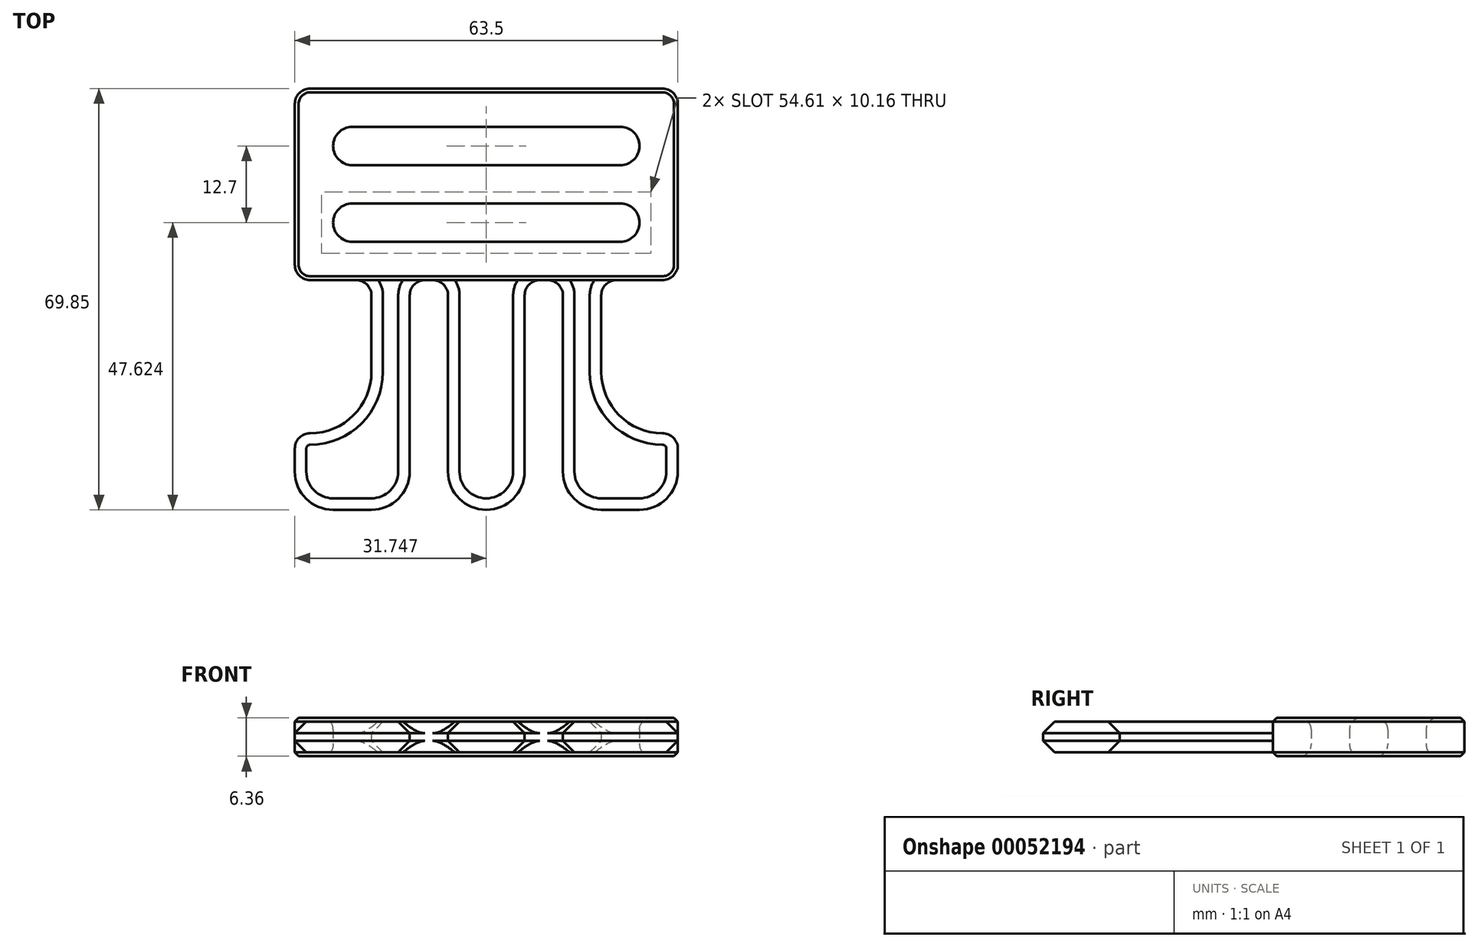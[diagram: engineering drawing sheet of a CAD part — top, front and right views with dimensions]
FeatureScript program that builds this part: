
annotation { "Feature Type Name" : "Feature", "Feature Type Description" : "" }
export const myFeature = defineFeature(function(context is Context, id is Id, definition is map)
    precondition{}
    {
        {
            var Q0;
            Q0=qCreatedBy(makeId("Top.planeOp"),FACE);
            var sketch = newSketch(context, id + "F0", { "sketchPlane" : qUnion([Q0])});
            skLineSegment(sketch, "E0", {"start": v(-60.65, -48.93) * mm, "end": v(-60.65, -45.12) * mm});
            skLineSegment(sketch, "E1", {"start": v(-58.11, 14.57) * mm, "end": v(0.3, 14.57) * mm});
            skLineSegment(sketch, "E2", {"start": v(2.85, 12.03) * mm, "end": v(2.85, -14.64) * mm});
            skLineSegment(sketch, "E3", {"start": v(-3.5, -55.28) * mm, "end": v(-9.85, -55.28) * mm});
            skLineSegment(sketch, "E4", {"start": v(-58.11, -42.58) * mm, "end": v(-58.11, -42.58) * mm});
            skLineSegment(sketch, "E5", {"start": v(-47.95, -32.42) * mm, "end": v(-47.95, -19.72) * mm});
            skLineSegment(sketch, "E6", {"start": v(-50.5, -17.18) * mm, "end": v(-58.11, -17.18) * mm});
            skLineSegment(sketch, "E7", {"start": v(-41.6, -48.93) * mm, "end": v(-41.6, -19.72) * mm});
            skLineSegment(sketch, "E8", {"start": v(-39.06, -17.18) * mm, "end": v(-37.8, -17.18) * mm});
            skLineSegment(sketch, "E9", {"start": v(-35.25, -19.72) * mm, "end": v(-35.25, -48.93) * mm});
            skLineSegment(sketch, "E10.MirrorCS", {"start": v(-22.55, -19.72) * mm, "end": v(-22.55, -48.93) * mm});
            skLineSegment(sketch, "E11.MirrorCS", {"start": v(-18.74, -17.18) * mm, "end": v(-20.01, -17.18) * mm});
            skLineSegment(sketch, "E12.MirrorCS", {"start": v(-16.2, -48.93) * mm, "end": v(-16.2, -19.72) * mm});
            skLineSegment(sketch, "E13.MirrorCS", {"start": v(-9.85, -32.42) * mm, "end": v(-9.85, -19.72) * mm});
            skLineSegment(sketch, "E14.MirrorCS", {"start": v(-7.31, -17.18) * mm, "end": v(0.3, -17.18) * mm});
            skLineSegment(sketch, "E15.MirrorCS", {"start": v(0.3, -42.58) * mm, "end": v(0.3, -42.58) * mm});
            skLineSegment(sketch, "E16", {"start": v(-54.3, -7.66) * mm, "end": v(-54.3, -7.66) * mm});
            skLineSegment(sketch, "E17", {"start": v(-51.13, -10.83) * mm, "end": v(-6.68, -10.83) * mm});
            skLineSegment(sketch, "E18", {"start": v(-3.5, -7.66) * mm, "end": v(-3.5, -7.66) * mm});
            skLineSegment(sketch, "E19", {"start": v(-6.68, 8.22) * mm, "end": v(-51.13, 8.22) * mm});
            skLineSegment(sketch, "E20.trimOffspring", {"start": v(-47.95, -55.28) * mm, "end": v(-54.3, -55.28) * mm});
            skLineSegment(sketch, "E21.trimOffspring", {"start": v(-60.65, -14.64) * mm, "end": v(-60.65, 12.03) * mm});
            skLineSegment(sketch, "E22.trimOffspring", {"start": v(2.85, -45.12) * mm, "end": v(2.85, -48.93) * mm});
            skLineSegment(sketch, "E23.trimOffspring", {"start": v(-28.9, -55.28) * mm, "end": v(-28.9, -55.28) * mm});
            skPoint(sketch, "E24.visualSharp", {"position": v(-47.95, -42.58) * mm});
            skArc(sketch, "E24.filletArc", {"start": v(-58.11, -42.58) * mm, "mid": v(-50.93, -39.6) * mm, "end": v(-47.95, -32.42) * mm});
            skPoint(sketch, "E25.visualSharp", {"position": v(-9.85, -42.58) * mm});
            skArc(sketch, "E25.filletArc", {"start": v(-9.85, -32.42) * mm, "mid": v(-6.88, -39.6) * mm, "end": v(0.3, -42.58) * mm});
            skPoint(sketch, "E26.visualSharp", {"position": v(2.85, -42.58) * mm});
            skArc(sketch, "E26.filletArc", {"start": v(2.85, -45.12) * mm, "mid": v(2.1, -43.32) * mm, "end": v(0.3, -42.58) * mm});
            skPoint(sketch, "E27.visualSharp", {"position": v(-60.65, -42.58) * mm});
            skArc(sketch, "E27.filletArc", {"start": v(-58.11, -42.58) * mm, "mid": v(-59.9, -43.32) * mm, "end": v(-60.65, -45.12) * mm});
            skPoint(sketch, "E28.visualSharp", {"position": v(-16.2, -55.28) * mm});
            skArc(sketch, "E28.filletArc", {"start": v(-16.2, -48.93) * mm, "mid": v(-14.34, -53.42) * mm, "end": v(-9.85, -55.28) * mm});
            skPoint(sketch, "E29.visualSharp", {"position": v(2.85, -55.28) * mm});
            skArc(sketch, "E29.filletArc", {"start": v(-3.5, -55.28) * mm, "mid": v(0.99, -53.42) * mm, "end": v(2.85, -48.93) * mm});
            skPoint(sketch, "E30.visualSharp", {"position": v(-60.65, -55.28) * mm});
            skArc(sketch, "E30.filletArc", {"start": v(-60.65, -48.93) * mm, "mid": v(-58.8, -53.42) * mm, "end": v(-54.3, -55.28) * mm});
            skPoint(sketch, "E31.visualSharp", {"position": v(-41.6, -55.28) * mm});
            skArc(sketch, "E31.filletArc", {"start": v(-47.95, -55.28) * mm, "mid": v(-43.46, -53.42) * mm, "end": v(-41.6, -48.93) * mm});
            skPoint(sketch, "E32.visualSharp", {"position": v(-35.25, -55.28) * mm});
            skArc(sketch, "E32.filletArc", {"start": v(-35.25, -48.93) * mm, "mid": v(-33.4, -53.42) * mm, "end": v(-28.9, -55.28) * mm});
            skPoint(sketch, "E33.visualSharp", {"position": v(-22.55, -55.28) * mm});
            skArc(sketch, "E33.filletArc", {"start": v(-28.9, -55.28) * mm, "mid": v(-24.41, -53.42) * mm, "end": v(-22.55, -48.93) * mm});
            skPoint(sketch, "E34.visualSharp", {"position": v(-47.95, -17.18) * mm});
            skArc(sketch, "E34.filletArc", {"start": v(-47.95, -19.72) * mm, "mid": v(-48.7, -17.92) * mm, "end": v(-50.5, -17.18) * mm});
            skPoint(sketch, "E35.visualSharp", {"position": v(-41.6, -17.18) * mm});
            skArc(sketch, "E35.filletArc", {"start": v(-39.06, -17.18) * mm, "mid": v(-40.86, -17.92) * mm, "end": v(-41.6, -19.72) * mm});
            skPoint(sketch, "E36.visualSharp", {"position": v(-35.25, -17.18) * mm});
            skArc(sketch, "E36.filletArc", {"start": v(-35.25, -19.72) * mm, "mid": v(-36, -17.92) * mm, "end": v(-37.8, -17.18) * mm});
            skPoint(sketch, "E37.visualSharp", {"position": v(-22.55, -17.18) * mm});
            skArc(sketch, "E37.filletArc", {"start": v(-20.01, -17.18) * mm, "mid": v(-21.8, -17.92) * mm, "end": v(-22.55, -19.72) * mm});
            skPoint(sketch, "E38.visualSharp", {"position": v(-16.2, -17.18) * mm});
            skArc(sketch, "E38.filletArc", {"start": v(-16.2, -19.72) * mm, "mid": v(-16.95, -17.92) * mm, "end": v(-18.74, -17.18) * mm});
            skPoint(sketch, "E39.visualSharp", {"position": v(-9.85, -17.18) * mm});
            skArc(sketch, "E39.filletArc", {"start": v(-7.31, -17.18) * mm, "mid": v(-9.1, -17.92) * mm, "end": v(-9.85, -19.72) * mm});
            skPoint(sketch, "E40.visualSharp", {"position": v(2.85, -17.18) * mm});
            skArc(sketch, "E40.filletArc", {"start": v(0.3, -17.18) * mm, "mid": v(2.1, -16.44) * mm, "end": v(2.85, -14.64) * mm});
            skPoint(sketch, "E41.visualSharp", {"position": v(-60.65, -17.18) * mm});
            skArc(sketch, "E41.filletArc", {"start": v(-60.65, -14.64) * mm, "mid": v(-59.9, -16.44) * mm, "end": v(-58.11, -17.18) * mm});
            skPoint(sketch, "E42.visualSharp", {"position": v(-60.65, 14.57) * mm});
            skArc(sketch, "E42.filletArc", {"start": v(-58.11, 14.57) * mm, "mid": v(-59.9, 13.83) * mm, "end": v(-60.65, 12.03) * mm});
            skPoint(sketch, "E43.visualSharp", {"position": v(2.85, 14.57) * mm});
            skArc(sketch, "E43.filletArc", {"start": v(2.85, 12.03) * mm, "mid": v(2.1, 13.83) * mm, "end": v(0.3, 14.57) * mm});
            skLineSegment(sketch, "E44", {"start": v(-51.13, 1.87) * mm, "end": v(-6.68, 1.87) * mm});
            skLineSegment(sketch, "E45", {"start": v(-51.13, -4.48) * mm, "end": v(-6.68, -4.48) * mm});
            skArc(sketch, "E46.filletArc", {"start": v(-51.13, -4.48) * mm, "mid": v(-53.37, -5.41) * mm, "end": v(-54.3, -7.66) * mm});
            skPoint(sketch, "E47.visualSharp", {"position": v(-54.3, -10.83) * mm});
            skArc(sketch, "E47.filletArc", {"start": v(-54.3, -7.66) * mm, "mid": v(-53.37, -9.9) * mm, "end": v(-51.13, -10.83) * mm});
            skArc(sketch, "E48.filletArc", {"start": v(-3.5, -7.66) * mm, "mid": v(-4.43, -5.41) * mm, "end": v(-6.68, -4.48) * mm});
            skPoint(sketch, "E49.visualSharp", {"position": v(-3.5, -10.83) * mm});
            skArc(sketch, "E49.filletArc", {"start": v(-6.68, -10.83) * mm, "mid": v(-4.43, -9.9) * mm, "end": v(-3.5, -7.66) * mm});
            skLineSegment(sketch, "E50", {"start": v(-54.3, 5.04) * mm, "end": v(-54.3, 5.04) * mm});
            skLineSegment(sketch, "E51", {"start": v(-3.5, 5.04) * mm, "end": v(-3.5, 5.04) * mm});
            skPoint(sketch, "E52.visualSharp", {"position": v(-54.3, 8.22) * mm});
            skArc(sketch, "E52.filletArc", {"start": v(-51.13, 8.22) * mm, "mid": v(-53.37, 7.29) * mm, "end": v(-54.3, 5.04) * mm});
            skPoint(sketch, "E53.visualSharp", {"position": v(-54.3, 1.87) * mm});
            skArc(sketch, "E53.filletArc", {"start": v(-54.3, 5.04) * mm, "mid": v(-53.37, 2.8) * mm, "end": v(-51.13, 1.87) * mm});
            skPoint(sketch, "E54.visualSharp", {"position": v(-3.5, 8.22) * mm});
            skArc(sketch, "E54.filletArc", {"start": v(-3.5, 5.04) * mm, "mid": v(-4.43, 7.29) * mm, "end": v(-6.68, 8.22) * mm});
            skPoint(sketch, "E55.visualSharp", {"position": v(-3.5, 1.87) * mm});
            skArc(sketch, "E55.filletArc", {"start": v(-6.68, 1.87) * mm, "mid": v(-4.43, 2.8) * mm, "end": v(-3.5, 5.04) * mm});
            skLineSegment(sketch, "E56", {"start": v(-50.5, -17.18) * mm, "end": v(-7.31, -17.18) * mm});
            skSolve(sketch);
        }
        {
            var Q0;
            Q0=makeQuery(id+"F0.imprint","IMPRINT",FACE,{"disambiguationData":[TD([[makeQuery(id+"F0.imprint","IMPRINT",EDGE,{"derivedFrom":sQuery(id+"F0.wireOp",EDGE,"E0")}),-1.0]])]});
            var Q1;
            Q1=makeQuery(id+"F0.imprint","IMPRINT",FACE,{"disambiguationData":[TD([[makeQuery(id+"F0.imprint","IMPRINT",EDGE,{"derivedFrom":sQuery(id+"F0.wireOp",EDGE,"E9")}),1.0]])]});
            var Q2;
            Q2=makeQuery(id+"F0.imprint","IMPRINT",FACE,{"disambiguationData":[TD([[makeQuery(id+"F0.imprint","IMPRINT",EDGE,{"derivedFrom":sQuery(id+"F0.wireOp",EDGE,"E3")}),-1.0]])]});
            extrude(context, id + "F1", {"entities" : qUnion([Q0, Q1, Q2]), "depth" : 2.54 * mm});
        }
        {
            var Q0;
            Q0=makeQuery(id+"F0.imprint","IMPRINT",FACE,{"disambiguationData":[TD([[makeQuery(id+"F0.imprint","IMPRINT",EDGE,{"derivedFrom":sQuery(id+"F0.wireOp",EDGE,"E1")}),-1.0]])]});
            extrude(context, id + "F2", {"entities" : qUnion([Q0]), "operationType" : NewBodyOperationType.ADD, "depth" : 3.17 * mm});
        }
        {
            var Q0;
            Q0=makeQuery(id+"F2.opExtrude","CAP_EDGE",EDGE,{"disambiguationData":[OSD([sQuery(id+"F0.wireOp",EDGE,"E6"),sQuery(id+"F0.wireOp",EDGE,"E14.MirrorCS"),sQuery(id+"F0.wireOp",EDGE,"E56")])],"isStart":false});
            chamfer(context, id + "F3", {"entities" : qUnion([Q0]), "width" : 0.64 * mm, "tangentPropagation" : true});
        }
        {
            var Q0;
            Q0=makeQuery(id+"F2.opExtrude","CAP_EDGE",EDGE,{"disambiguationData":[OSD([sQuery(id+"F0.wireOp",EDGE,"E45")])],"isStart":false});
            var Q1;
            Q1=makeQuery(id+"F2.opExtrude","CAP_EDGE",EDGE,{"disambiguationData":[OSD([sQuery(id+"F0.wireOp",EDGE,"E19")])],"isStart":false});
            fillet(context, id + "F4", {"entities" : qUnion([Q0, Q1]), "radius" : 1.9 * mm, "tangentPropagation" : true, "allowEdgeOverflow" : false});
        }
        {
            var Q0;
            Q0=makeQuery(id+"F1.opExtrude","CAP_EDGE",EDGE,{"disambiguationData":[OSD([sQuery(id+"F0.wireOp",EDGE,"E5")])],"isStart":false});
            var Q1;
            Q1=makeQuery(id+"F1.opExtrude","CAP_EDGE",EDGE,{"disambiguationData":[OSD([sQuery(id+"F0.wireOp",EDGE,"E9")])],"isStart":false});
            var Q2;
            Q2=makeQuery(id+"F1.opExtrude","CAP_EDGE",EDGE,{"disambiguationData":[OSD([sQuery(id+"F0.wireOp",EDGE,"E12.MirrorCS")])],"isStart":false});
            chamfer(context, id + "F5", {"entities" : qUnion([Q0, Q1, Q2]), "width" : 1.9 * mm, "tangentPropagation" : true});
        }
        {
            var Q0;
            Q0=makeQuery(id+"F1.opExtrude","SWEPT_BODY",BODY,{"disambiguationData":[OSD([sQuery(id+"F0.wireOp",EDGE,"E0"),sQuery(id+"F0.wireOp",EDGE,"E5"),sQuery(id+"F0.wireOp",EDGE,"E7"),sQuery(id+"F0.wireOp",EDGE,"E20.trimOffspring"),sQuery(id+"F0.wireOp",EDGE,"E24.filletArc"),sQuery(id+"F0.wireOp",EDGE,"E27.filletArc"),sQuery(id+"F0.wireOp",EDGE,"E30.filletArc"),sQuery(id+"F0.wireOp",EDGE,"E31.filletArc"),sQuery(id+"F0.wireOp",EDGE,"E34.filletArc"),sQuery(id+"F0.wireOp",EDGE,"E35.filletArc"),sQuery(id+"F0.wireOp",EDGE,"E56")])]});
            var Q1;
            Q1=qCreatedBy(makeId("Top.planeOp"),FACE);
            mirror(context, id + "F6", {"operationType" : NewBodyOperationType.ADD, "entities" : qUnion([Q0]), "mirrorPlane" : qUnion([Q1])});
        }
    });
